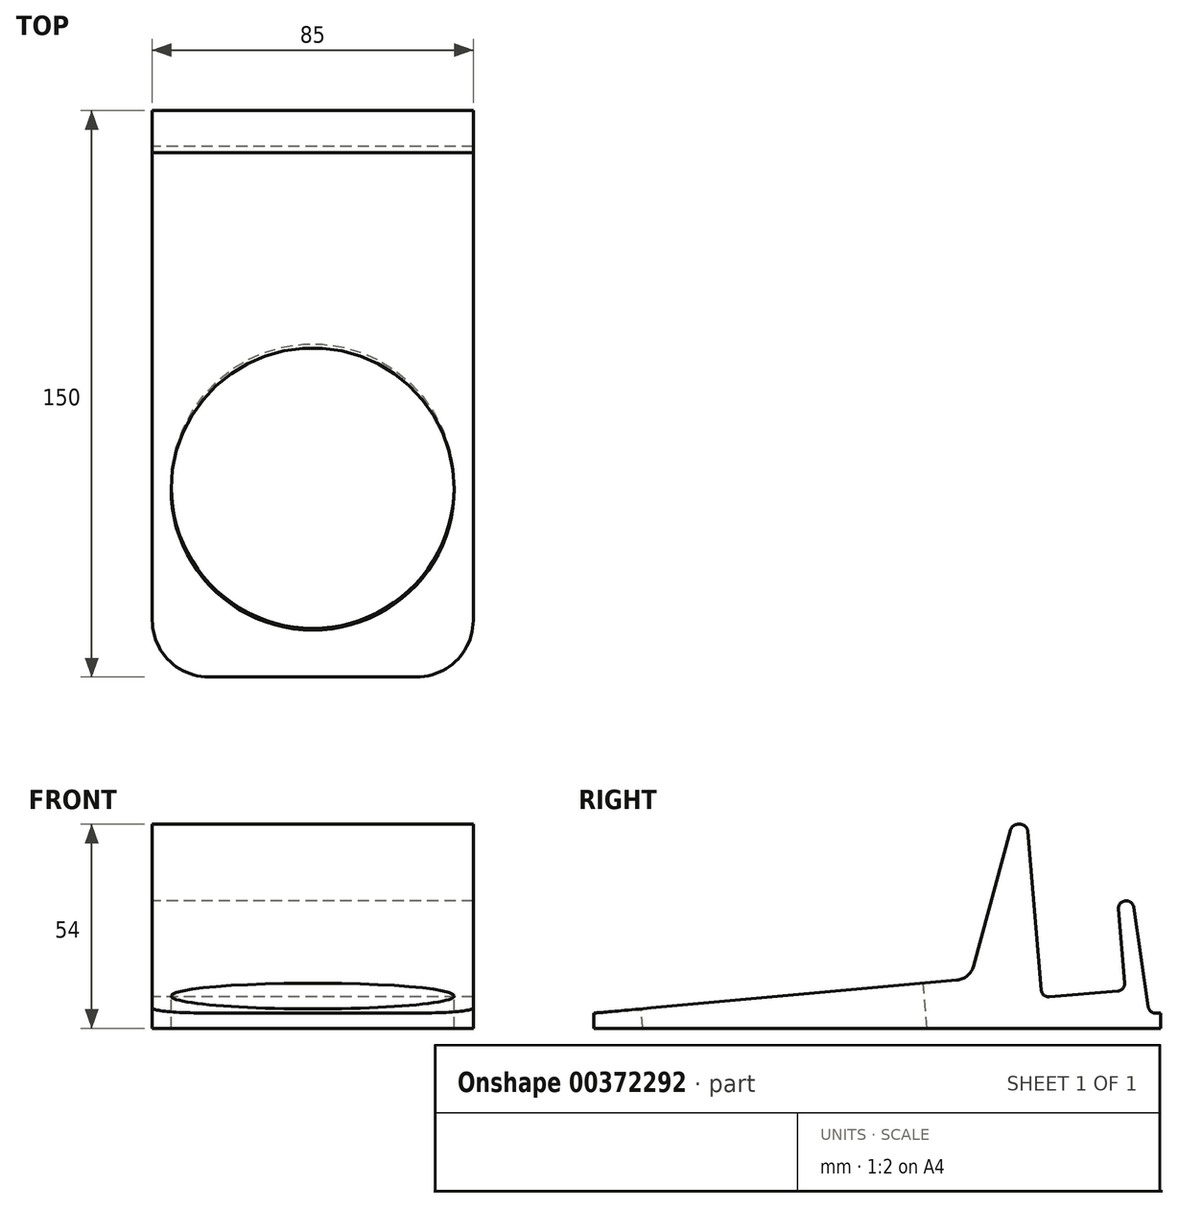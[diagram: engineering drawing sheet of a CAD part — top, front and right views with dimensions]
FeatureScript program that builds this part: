
annotation { "Feature Type Name" : "Feature", "Feature Type Description" : "" }
export const myFeature = defineFeature(function(context is Context, id is Id, definition is map)
    precondition{}
    {
        {
            var Q0;
            Q0=qCreatedBy(makeId("Right.planeOp"),FACE);
            var sketch = newSketch(context, id + "F0", { "sketchPlane" : qUnion([Q0])});
            skLineSegment(sketch, "E0", {"start": v(0, 0) * mm, "end": v(0, 4) * mm});
            skLineSegment(sketch, "E1", {"start": v(150, 4) * mm, "end": v(150, 0) * mm});
            skLineSegment(sketch, "E2", {"start": v(150, 0) * mm, "end": v(0, 0) * mm});
            skLineSegment(sketch, "E3", {"start": v(150, 4) * mm, "end": v(148.73, 4) * mm});
            skLineSegment(sketch, "E4", {"start": v(146.75, 5.71) * mm, "end": v(142.68, 34) * mm});
            skLineSegment(sketch, "E5", {"start": v(142.68, 34) * mm, "end": v(138.72, 33.43) * mm});
            skLineSegment(sketch, "E6", {"start": v(138.72, 33.43) * mm, "end": v(140.53, 12) * mm});
            skPoint(sketch, "E6.endSnap0", {"position": v(140.7, 33.71) * mm});
            skLineSegment(sketch, "E7", {"start": v(138.7, 9.83) * mm, "end": v(120.59, 8.3) * mm});
            skLineSegment(sketch, "E8", {"start": v(118.43, 10.13) * mm, "end": v(114.72, 54) * mm});
            skLineSegment(sketch, "E9", {"start": v(114.72, 54) * mm, "end": v(110.72, 54) * mm});
            skLineSegment(sketch, "E10", {"start": v(110.72, 54) * mm, "end": v(100.47, 16.42) * mm});
            skLineSegment(sketch, "E11", {"start": v(96.1, 12.76) * mm, "end": v(0, 4) * mm});
            skPoint(sketch, "E12.visualSharp", {"position": v(147, 4) * mm});
            skArc(sketch, "E12.filletArc", {"start": v(146.75, 5.71) * mm, "mid": v(147.42, 4.49) * mm, "end": v(148.73, 4) * mm});
            skPoint(sketch, "E13.visualSharp", {"position": v(99.56, 13.07) * mm});
            skArc(sketch, "E13.filletArc", {"start": v(96.1, 12.76) * mm, "mid": v(98.86, 13.9) * mm, "end": v(100.47, 16.42) * mm});
            skPoint(sketch, "E14.visualSharp", {"position": v(118.6, 8.13) * mm});
            skArc(sketch, "E14.filletArc", {"start": v(118.43, 10.13) * mm, "mid": v(119.13, 8.77) * mm, "end": v(120.59, 8.3) * mm});
            skPoint(sketch, "E15.visualSharp", {"position": v(140.7, 10) * mm});
            skArc(sketch, "E15.filletArc", {"start": v(138.7, 9.83) * mm, "mid": v(140.06, 10.53) * mm, "end": v(140.53, 12) * mm});
            skSolve(sketch);
        }
        {
            var Q0;
            Q0 = qSketchRegion(id + "F0", true);
            extrude(context, id + "F1", {"entities" : qUnion([Q0]), "depth" : 85 * mm});
        }
        {
            var Q0;
            Q0=makeQuery(id+"F1.opExtrude","CAP_EDGE",EDGE,{"disambiguationData":[OSD([sQuery(id+"F0.wireOp",EDGE,"E0")])],"isStart":false});
            var Q1;
            Q1=makeQuery(id+"F1.opExtrude","CAP_EDGE",EDGE,{"disambiguationData":[OSD([sQuery(id+"F0.wireOp",EDGE,"E0")])],"isStart":true});
            fillet(context, id + "F2", {"entities" : qUnion([Q0, Q1]), "radius" : 15 * mm, "tangentPropagation" : true, "allowEdgeOverflow" : false});
        }
        {
            var Q0;
            Q0=makeQuery(id+"F1.opExtrude","SWEPT_EDGE",EDGE,{"disambiguationData":[OSD([sQuery(id+"F0.wireOp",EDGE,"E9"),sQuery(id+"F0.wireOp",EDGE,"E10")])]});
            var Q1;
            Q1=makeQuery(id+"F1.opExtrude","SWEPT_EDGE",EDGE,{"disambiguationData":[OSD([sQuery(id+"F0.wireOp",EDGE,"E8"),sQuery(id+"F0.wireOp",EDGE,"E9")])]});
            var Q2;
            Q2=makeQuery(id+"F1.opExtrude","SWEPT_EDGE",EDGE,{"disambiguationData":[OSD([sQuery(id+"F0.wireOp",EDGE,"E5"),sQuery(id+"F0.wireOp",EDGE,"E6")])]});
            var Q3;
            Q3=makeQuery(id+"F1.opExtrude","SWEPT_EDGE",EDGE,{"disambiguationData":[OSD([sQuery(id+"F0.wireOp",EDGE,"E4"),sQuery(id+"F0.wireOp",EDGE,"E5")])]});
            fillet(context, id + "F3", {"entities" : qUnion([Q0, Q1, Q2, Q3]), "radius" : 2 * mm, "tangentPropagation" : true, "allowEdgeOverflow" : false});
        }
        {
            var Q0;
            Q0=makeQuery(id+"F1.opExtrude","SWEPT_BODY",BODY,{"disambiguationData":[OSD([sQuery(id+"F0.wireOp",EDGE,"E0"),sQuery(id+"F0.wireOp",EDGE,"E1"),sQuery(id+"F0.wireOp",EDGE,"E2"),sQuery(id+"F0.wireOp",EDGE,"E3"),sQuery(id+"F0.wireOp",EDGE,"E4"),sQuery(id+"F0.wireOp",EDGE,"E5"),sQuery(id+"F0.wireOp",EDGE,"E6"),sQuery(id+"F0.wireOp",EDGE,"E7"),sQuery(id+"F0.wireOp",EDGE,"E8"),sQuery(id+"F0.wireOp",EDGE,"E9"),sQuery(id+"F0.wireOp",EDGE,"E10"),sQuery(id+"F0.wireOp",EDGE,"E11"),sQuery(id+"F0.wireOp",EDGE,"E12.filletArc"),sQuery(id+"F0.wireOp",EDGE,"E13.filletArc"),sQuery(id+"F0.wireOp",EDGE,"E14.filletArc"),sQuery(id+"F0.wireOp",EDGE,"E15.filletArc")])]});
            transform(context, id + "F4", {"entities" : qUnion([Q0]), "transformType" : TransformType.TRANSLATION_3D, "dx" : 0 * mm, "dy" : 0 * mm, "dz" : 0 * mm, "makeCopy" : true});
        }
        {
            var Q0;
            Q0=makeQuery(id+"F4.opPattern","COPY",FACE,{"derivedFrom":makeQuery(id+"F1.opExtrude","SWEPT_FACE",FACE,{"disambiguationData":[OSD([sQuery(id+"F0.wireOp",EDGE,"E11")])]}),"instanceName":"1"});
            var sketch = newSketch(context, id + "F5", { "sketchPlane" : qUnion([Q0])});
            skCircle(sketch, "E16", {"center": v(42.5, 50.36) * mm, "radius": 37.5 * mm});
            skSolve(sketch);
        }
        {
            var Q0;
            Q0 = qSketchRegion(id + "F5", true);
            extrude(context, id + "F6", {"entities" : qUnion([Q0]), "operationType" : NewBodyOperationType.REMOVE, "oppositeDirection" : true, "depth" : 25 * mm});
        }
        {
            var Q0;
            Q0=makeQuery(id+"F1.opExtrude","SWEPT_BODY",BODY,{"disambiguationData":[OSD([sQuery(id+"F0.wireOp",EDGE,"E0"),sQuery(id+"F0.wireOp",EDGE,"E1"),sQuery(id+"F0.wireOp",EDGE,"E2"),sQuery(id+"F0.wireOp",EDGE,"E3"),sQuery(id+"F0.wireOp",EDGE,"E4"),sQuery(id+"F0.wireOp",EDGE,"E5"),sQuery(id+"F0.wireOp",EDGE,"E6"),sQuery(id+"F0.wireOp",EDGE,"E7"),sQuery(id+"F0.wireOp",EDGE,"E8"),sQuery(id+"F0.wireOp",EDGE,"E9"),sQuery(id+"F0.wireOp",EDGE,"E10"),sQuery(id+"F0.wireOp",EDGE,"E11"),sQuery(id+"F0.wireOp",EDGE,"E12.filletArc"),sQuery(id+"F0.wireOp",EDGE,"E13.filletArc"),sQuery(id+"F0.wireOp",EDGE,"E14.filletArc"),sQuery(id+"F0.wireOp",EDGE,"E15.filletArc")])]});
            transform(context, id + "F7", {"entities" : qUnion([Q0]), "transformType" : TransformType.TRANSLATION_3D, "dx" : 0 * mm, "dy" : 0 * mm, "dz" : 0 * mm, "makeCopy" : true});
        }
        {
            var Q0;
            Q0=makeQuery(id+"F1.opExtrude","SWEPT_BODY",BODY,{"disambiguationData":[OSD([sQuery(id+"F0.wireOp",EDGE,"E0"),sQuery(id+"F0.wireOp",EDGE,"E1"),sQuery(id+"F0.wireOp",EDGE,"E2"),sQuery(id+"F0.wireOp",EDGE,"E3"),sQuery(id+"F0.wireOp",EDGE,"E4"),sQuery(id+"F0.wireOp",EDGE,"E5"),sQuery(id+"F0.wireOp",EDGE,"E6"),sQuery(id+"F0.wireOp",EDGE,"E7"),sQuery(id+"F0.wireOp",EDGE,"E8"),sQuery(id+"F0.wireOp",EDGE,"E9"),sQuery(id+"F0.wireOp",EDGE,"E10"),sQuery(id+"F0.wireOp",EDGE,"E11"),sQuery(id+"F0.wireOp",EDGE,"E12.filletArc"),sQuery(id+"F0.wireOp",EDGE,"E13.filletArc"),sQuery(id+"F0.wireOp",EDGE,"E14.filletArc"),sQuery(id+"F0.wireOp",EDGE,"E15.filletArc")])]});
            deleteBodies(context, id + "F8", {"entities" : qUnion([Q0])});
        }
        {
            var Q0;
            Q0=makeQuery(id+"F4.opPattern","COPY",BODY,{"derivedFrom":makeQuery(id+"F1.opExtrude","SWEPT_BODY",BODY,{"disambiguationData":[OSD([sQuery(id+"F0.wireOp",EDGE,"E0"),sQuery(id+"F0.wireOp",EDGE,"E1"),sQuery(id+"F0.wireOp",EDGE,"E2"),sQuery(id+"F0.wireOp",EDGE,"E3"),sQuery(id+"F0.wireOp",EDGE,"E4"),sQuery(id+"F0.wireOp",EDGE,"E5"),sQuery(id+"F0.wireOp",EDGE,"E6"),sQuery(id+"F0.wireOp",EDGE,"E7"),sQuery(id+"F0.wireOp",EDGE,"E8"),sQuery(id+"F0.wireOp",EDGE,"E9"),sQuery(id+"F0.wireOp",EDGE,"E10"),sQuery(id+"F0.wireOp",EDGE,"E11"),sQuery(id+"F0.wireOp",EDGE,"E12.filletArc"),sQuery(id+"F0.wireOp",EDGE,"E13.filletArc"),sQuery(id+"F0.wireOp",EDGE,"E14.filletArc"),sQuery(id+"F0.wireOp",EDGE,"E15.filletArc")])]}),"instanceName":"1"});
            deleteBodies(context, id + "F9", {"entities" : qUnion([Q0])});
        }
    });
